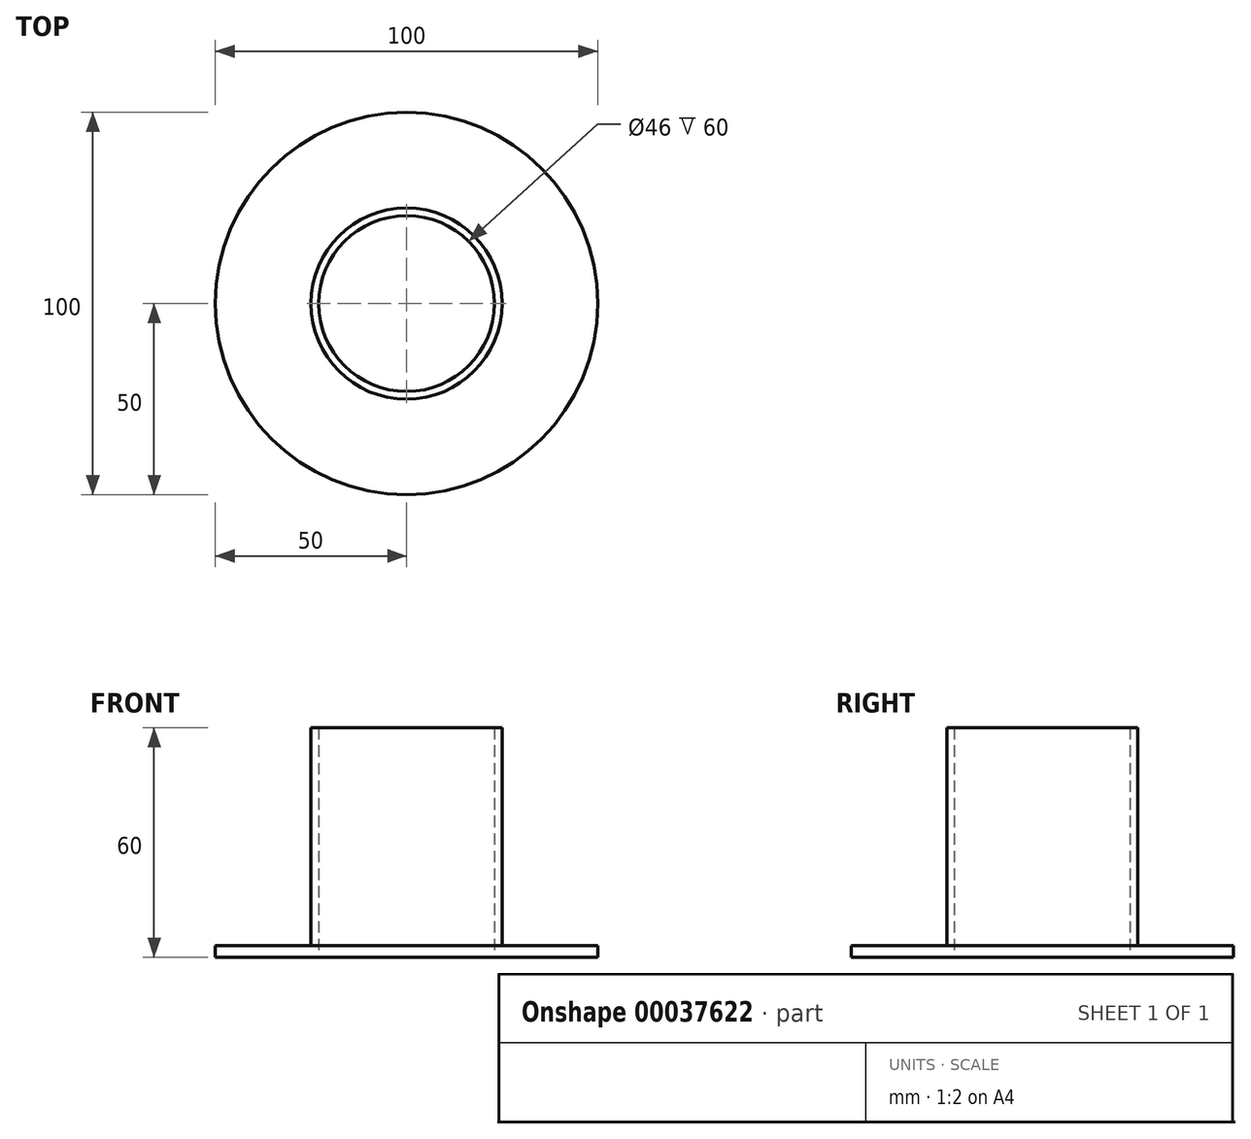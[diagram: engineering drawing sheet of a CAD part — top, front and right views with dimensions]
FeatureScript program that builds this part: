
annotation { "Feature Type Name" : "Feature", "Feature Type Description" : "" }
export const myFeature = defineFeature(function(context is Context, id is Id, definition is map)
    precondition{}
    {
        {
            var Q0;
            Q0=qCreatedBy(makeId("Top.planeOp"),FACE);
            var sketch = newSketch(context, id + "F0", { "sketchPlane" : qUnion([Q0])});
            skCircle(sketch, "E0", {"center": v(0, 0) * mm, "radius": 50 * mm});
            skSolve(sketch);
        }
        {
            var Q0;
            Q0 = qSketchRegion(id + "F0", true);
            extrude(context, id + "F1", {"entities" : qUnion([Q0]), "depth" : 3 * mm});
        }
        {
            var Q0;
            Q0=qCreatedBy(makeId("Top.planeOp"),FACE);
            var sketch = newSketch(context, id + "F2", { "sketchPlane" : qUnion([Q0])});
            skCircle(sketch, "E1", {"center": v(0, 0) * mm, "radius": 25 * mm});
            skSolve(sketch);
        }
        {
            var Q0;
            Q0 = qSketchRegion(id + "F2", true);
            extrude(context, id + "F3", {"entities" : qUnion([Q0]), "operationType" : NewBodyOperationType.ADD, "depth" : 60 * mm});
        }
        {
            var Q0;
            Q0=qCreatedBy(makeId("Top.planeOp"),FACE);
            var sketch = newSketch(context, id + "F4", { "sketchPlane" : qUnion([Q0])});
            skCircle(sketch, "E2", {"center": v(0, 0) * mm, "radius": 23 * mm});
            skSolve(sketch);
        }
        {
            var Q0;
            Q0 = qSketchRegion(id + "F4", true);
            extrude(context, id + "F5", {"entities" : qUnion([Q0]), "operationType" : NewBodyOperationType.REMOVE, "depth" : 60 * mm});
        }
    });
